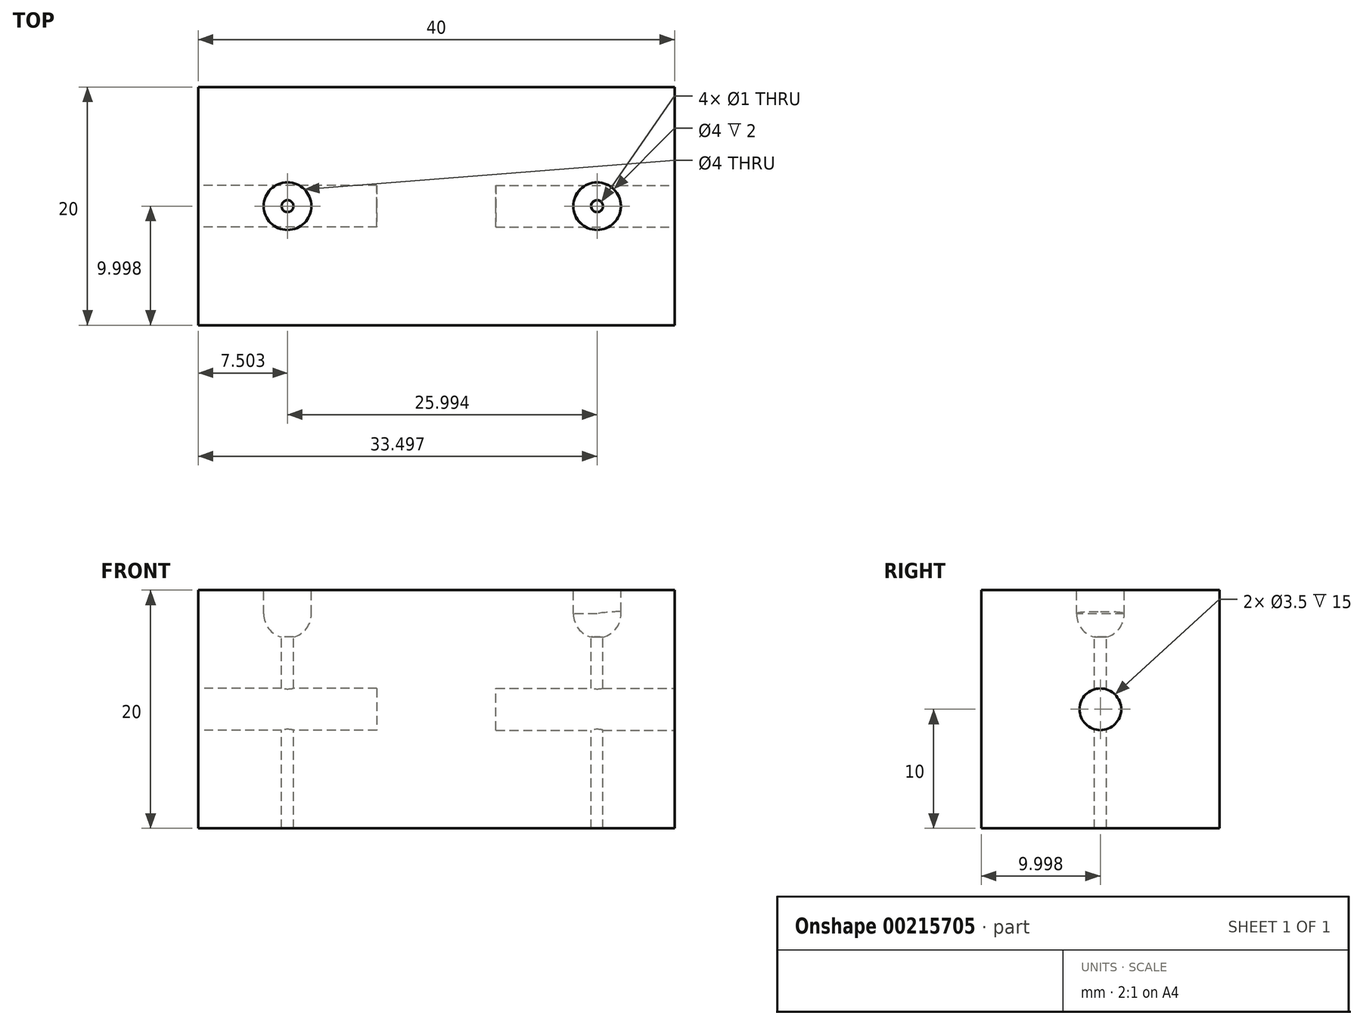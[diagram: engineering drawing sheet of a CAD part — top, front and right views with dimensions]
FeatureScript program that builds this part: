
annotation { "Feature Type Name" : "Feature", "Feature Type Description" : "" }
export const myFeature = defineFeature(function(context is Context, id is Id, definition is map)
    precondition{}
    {
        {
            var Q0;
            Q0=qCreatedBy(makeId("Top.planeOp"),FACE);
            var sketch = newSketch(context, id + "F0", { "sketchPlane" : qUnion([Q0])});
            skLineSegment(sketch, "E0.bottom", {"start": v(-20.5, 16.28) * mm, "end": v(19.5, 16.28) * mm});
            skLineSegment(sketch, "E0.top", {"start": v(-20.5, -3.72) * mm, "end": v(19.5, -3.72) * mm});
            skLineSegment(sketch, "E0.left", {"start": v(-20.5, 16.28) * mm, "end": v(-20.5, -3.72) * mm});
            skLineSegment(sketch, "E0.right", {"start": v(19.5, 16.28) * mm, "end": v(19.5, -3.72) * mm});
            skSolve(sketch);
        }
        {
            var Q0;
            Q0 = qSketchRegion(id + "F0", true);
            extrude(context, id + "F1", {"entities" : qUnion([Q0]), "depth" : 20 * mm});
        }
        {
            var Q0;
            Q0=makeQuery(id+"F1.opExtrude","SWEPT_FACE",FACE,{"disambiguationData":[OSD([sQuery(id+"F0.wireOp",EDGE,"E0.left")])]});
            var sketch = newSketch(context, id + "F2", { "sketchPlane" : qUnion([Q0])});
            skCircle(sketch, "E1", {"center": v(-6.28, 10) * mm, "radius": 1.75 * mm});
            skSolve(sketch);
        }
        {
            var Q0;
            Q0 = qSketchRegion(id + "F2", true);
            extrude(context, id + "F3", {"entities" : qUnion([Q0]), "operationType" : NewBodyOperationType.REMOVE, "oppositeDirection" : true, "depth" : 15 * mm});
        }
        {
            var Q0;
            Q0=makeQuery(id+"F1.opExtrude","SWEPT_FACE",FACE,{"disambiguationData":[OSD([sQuery(id+"F0.wireOp",EDGE,"E0.right")])]});
            var sketch = newSketch(context, id + "F4", { "sketchPlane" : qUnion([Q0])});
            skCircle(sketch, "E2", {"center": v(6.28, 10) * mm, "radius": 1.75 * mm});
            skSolve(sketch);
        }
        {
            var Q0;
            Q0 = qSketchRegion(id + "F4", true);
            extrude(context, id + "F5", {"entities" : qUnion([Q0]), "operationType" : NewBodyOperationType.REMOVE, "oppositeDirection" : true, "depth" : 15 * mm});
        }
        {
            var Q0;
            Q0=makeQuery(id+"F1.opExtrude","CAP_FACE",FACE,{"disambiguationData":[OSD([sQuery(id+"F0.wireOp",EDGE,"E0.bottom"),sQuery(id+"F0.wireOp",EDGE,"E0.top"),sQuery(id+"F0.wireOp",EDGE,"E0.left"),sQuery(id+"F0.wireOp",EDGE,"E0.right")])],"isStart":false});
            var sketch = newSketch(context, id + "F6", { "sketchPlane" : qUnion([Q0])});
            skCircle(sketch, "E3", {"center": v(-13, 6.28) * mm, "radius": 0.5 * mm});
            skCircle(sketch, "E4.MirrorC", {"center": v(13, 6.28) * mm, "radius": 0.5 * mm});
            skSolve(sketch);
        }
        {
            var Q0;
            Q0 = qSketchRegion(id + "F6", true);
            extrude(context, id + "F7", {"entities" : qUnion([Q0]), "operationType" : NewBodyOperationType.REMOVE, "endBound" : BoundingType.THROUGH_ALL, "oppositeDirection" : true, "depth" : 25 * mm});
        }
        {
            var Q0;
            Q0=makeQuery(id+"F1.opExtrude","CAP_FACE",FACE,{"disambiguationData":[OSD([sQuery(id+"F0.wireOp",EDGE,"E0.bottom"),sQuery(id+"F0.wireOp",EDGE,"E0.top"),sQuery(id+"F0.wireOp",EDGE,"E0.left"),sQuery(id+"F0.wireOp",EDGE,"E0.right")])],"isStart":false});
            var sketch = newSketch(context, id + "F8", { "sketchPlane" : qUnion([Q0])});
            skCircle(sketch, "E5", {"center": v(-13, 6.28) * mm, "radius": 2 * mm});
            skSolve(sketch);
        }
        {
            var Q0;
            Q0 = qSketchRegion(id + "F8", true);
            extrude(context, id + "F9", {"entities" : qUnion([Q0]), "operationType" : NewBodyOperationType.REMOVE, "oppositeDirection" : true, "depth" : 2 * mm});
        }
        {
            var Q0;
            Q0=makeQuery(id+"F9.boolean.opBoolean","COPY",FACE,{"derivedFrom":makeQuery(id+"F9.opExtrude","CAP_FACE",FACE,{"disambiguationData":[OSD([sQuery(id+"F8.wireOp",EDGE,"E5")])],"isStart":false})});
            var sketch = newSketch(context, id + "F10", { "sketchPlane" : qUnion([Q0])});
            skLineSegment(sketch, "E6", {"start": v(-13, 8.28) * mm, "end": v(-13, 4.28) * mm});
            skArc(sketch, "E7", {"start": v(-13, 8.28) * mm, "mid": v(-15, 6.28) * mm, "end": v(-13, 4.28) * mm});
            skSolve(sketch);
        }
        {
            var Q0;
            Q0 = qSketchRegion(id + "F10", true);
            var Q1;
            Q1=sQuery(id+"F10.wireOp",EDGE,"E6");
            revolve(context, id + "F11", {"operationType" : NewBodyOperationType.REMOVE, "entities" : qUnion([Q0]), "axis" : qUnion([Q1]), "revolveType" : RevolveType.FULL, "oppositeDirection" : true});
        }
        {
            var Q0;
            Q0=makeQuery(id+"F1.opExtrude","CAP_FACE",FACE,{"disambiguationData":[OSD([sQuery(id+"F0.wireOp",EDGE,"E0.bottom"),sQuery(id+"F0.wireOp",EDGE,"E0.top"),sQuery(id+"F0.wireOp",EDGE,"E0.left"),sQuery(id+"F0.wireOp",EDGE,"E0.right")])],"isStart":false});
            var sketch = newSketch(context, id + "F12", { "sketchPlane" : qUnion([Q0])});
            skCircle(sketch, "E8", {"center": v(13, 6.28) * mm, "radius": 2 * mm});
            skSolve(sketch);
        }
        {
            var Q0;
            Q0 = qSketchRegion(id + "F12", true);
            extrude(context, id + "F13", {"entities" : qUnion([Q0]), "operationType" : NewBodyOperationType.REMOVE, "oppositeDirection" : true, "depth" : 2 * mm});
        }
        {
            var Q0;
            Q0=makeQuery(id+"F13.boolean.opBoolean","COPY",FACE,{"derivedFrom":makeQuery(id+"F13.opExtrude","CAP_FACE",FACE,{"disambiguationData":[OSD([sQuery(id+"F12.wireOp",EDGE,"E8")])],"isStart":false})});
            var sketch = newSketch(context, id + "F14", { "sketchPlane" : qUnion([Q0])});
            skLineSegment(sketch, "E9", {"start": v(13, 8.28) * mm, "end": v(13, 4.28) * mm});
            skArc(sketch, "E10", {"start": v(13, 8.28) * mm, "mid": v(11, 6.28) * mm, "end": v(13, 4.28) * mm});
            skSolve(sketch);
        }
        {
            var Q0;
            Q0 = qSketchRegion(id + "F14", true);
            var Q1;
            Q1=sQuery(id+"F14.wireOp",EDGE,"E9");
            revolve(context, id + "F15", {"operationType" : NewBodyOperationType.REMOVE, "entities" : qUnion([Q0]), "axis" : qUnion([Q1]), "revolveType" : RevolveType.FULL, "oppositeDirection" : true});
        }
    });
